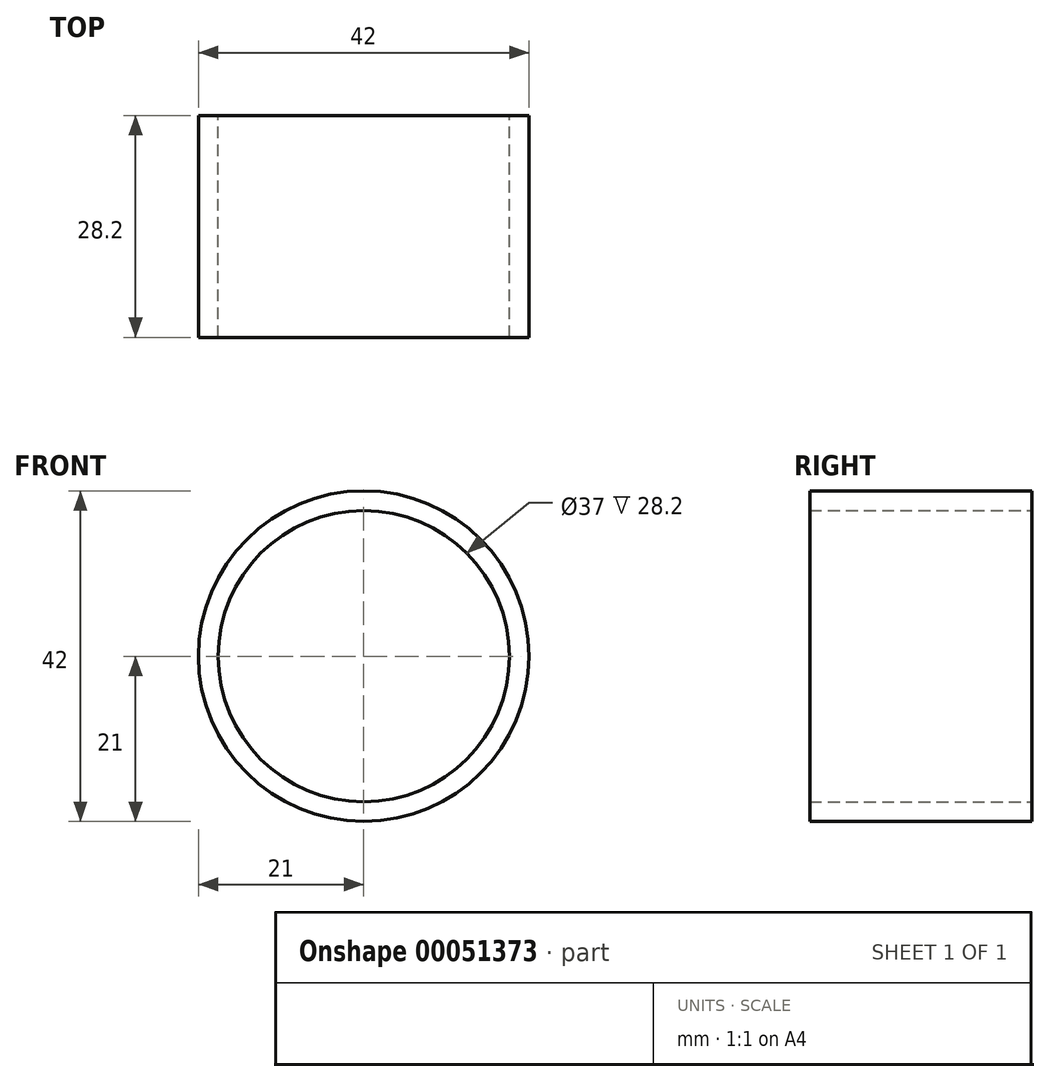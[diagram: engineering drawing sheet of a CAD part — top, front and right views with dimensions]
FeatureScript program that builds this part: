
annotation { "Feature Type Name" : "Feature", "Feature Type Description" : "" }
export const myFeature = defineFeature(function(context is Context, id is Id, definition is map)
    precondition{}
    {
        {
            var Q0;
            Q0=qCreatedBy(makeId("Front.planeOp"),FACE);
            var sketch = newSketch(context, id + "F0", { "sketchPlane" : qUnion([Q0])});
            skCircle(sketch, "E0", {"center": v(0, 0) * mm, "radius": 21 * mm});
            skCircle(sketch, "E1", {"center": v(0, 0) * mm, "radius": 18.5 * mm});
            skSolve(sketch);
        }
        {
            var Q0;
            Q0=qSketchRegion(id+"F0",true);
            extrude(context, id + "F1", {"entities" : qUnion([Q0]), "depth" : 14.1 * mm, "hasSecondDirection" : true, "secondDirectionOppositeDirection" : true, "secondDirectionDepth" : 14.1 * mm});
        }
    });
